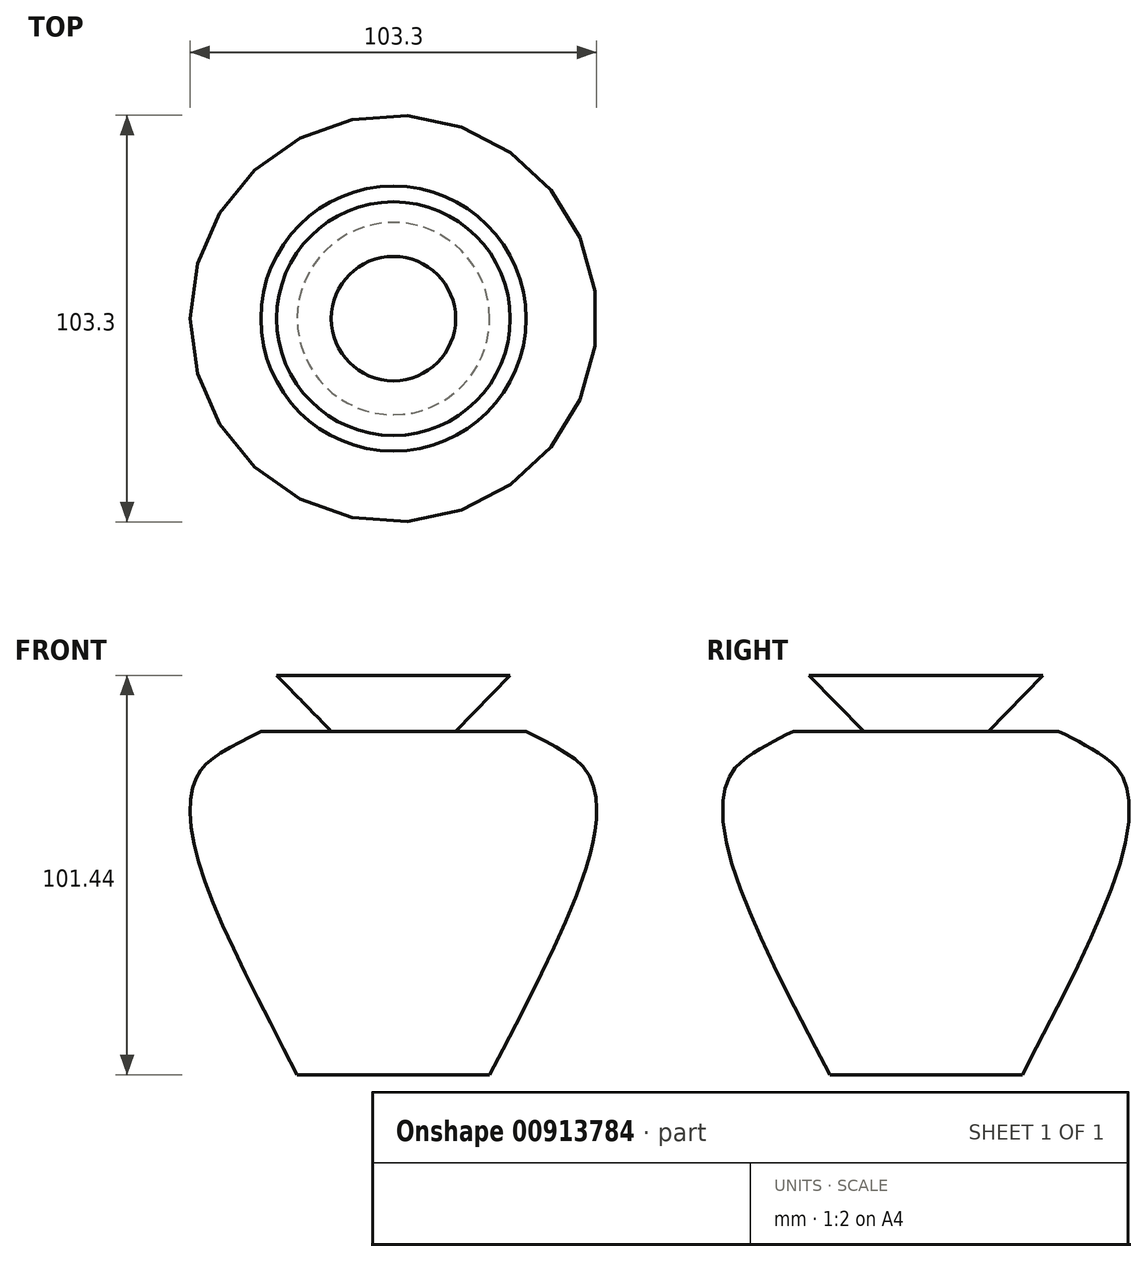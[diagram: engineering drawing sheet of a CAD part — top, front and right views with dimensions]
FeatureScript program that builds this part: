
annotation { "Feature Type Name" : "Feature", "Feature Type Description" : "" }
export const myFeature = defineFeature(function(context is Context, id is Id, definition is map)
    precondition{}
    {
        {
            var Q0;
            Q0=qCreatedBy(makeId("Front.planeOp"),FACE);
            var sketch = newSketch(context, id + "F0", { "sketchPlane" : qUnion([Q0])});
            skLineSegment(sketch, "E0", {"start": v(0, 45.86) * mm, "end": v(29.68, 45.86) * mm});
            skLineSegment(sketch, "E1", {"start": v(29.68, 45.86) * mm, "end": v(15.8, 31.68) * mm});
            skLineSegment(sketch, "E2", {"start": v(15.8, 31.68) * mm, "end": v(33.68, 31.68) * mm});
            skPoint(sketch, "E3.5.internal.snap0", {"position": v(22.74, 38.77) * mm});
            skFitSpline(sketch, "E4", {"points": [v(33.68, 31.68) * mm, v(44.78, 25.51) * mm, v(50.03, 19.96) * mm, v(50.64, 3) * mm, v(24.43, -55.58) * mm], "startDerivative": vector(62.78, -32.23) * mm, "endDerivative": vector(-79.42, -151.41) * mm});
            skLineSegment(sketch, "E5", {"start": v(24.43, -55.58) * mm, "end": v(0, -55.58) * mm});
            skLineSegment(sketch, "E6", {"start": v(0, 58.2) * mm, "end": v(0, -61.74) * mm});
            skLineSegment(sketch, "E7", {"start": v(0, 58.2) * mm, "end": v(0, -61.74) * mm, "construction": true});
            skSolve(sketch);
        }
        {
            var Q0;
            Q0=sQuery(id+"F0.wireOp",EDGE,"E0");
            var Q1;
            Q1=sQuery(id+"F0.wireOp",EDGE,"E1");
            var Q2;
            Q2=sQuery(id+"F0.wireOp",EDGE,"E2");
            var Q3;
            Q3=sQuery(id+"F0.wireOp",EDGE,"E4");
            var Q4;
            Q4=sQuery(id+"F0.wireOp",EDGE,"E5");
            var Q5;
            Q5=sQuery(id+"F0.wireOp",EDGE,"E6");
            revolve(context, id + "F1", {"bodyType" : ToolBodyType.SURFACE, "surfaceOperationType" : NewSurfaceOperationType.NEW, "surfaceEntities" : qUnion([Q0, Q1, Q2, Q3, Q4]), "axis" : qUnion([Q5]), "revolveType" : RevolveType.FULL});
        }
    });
